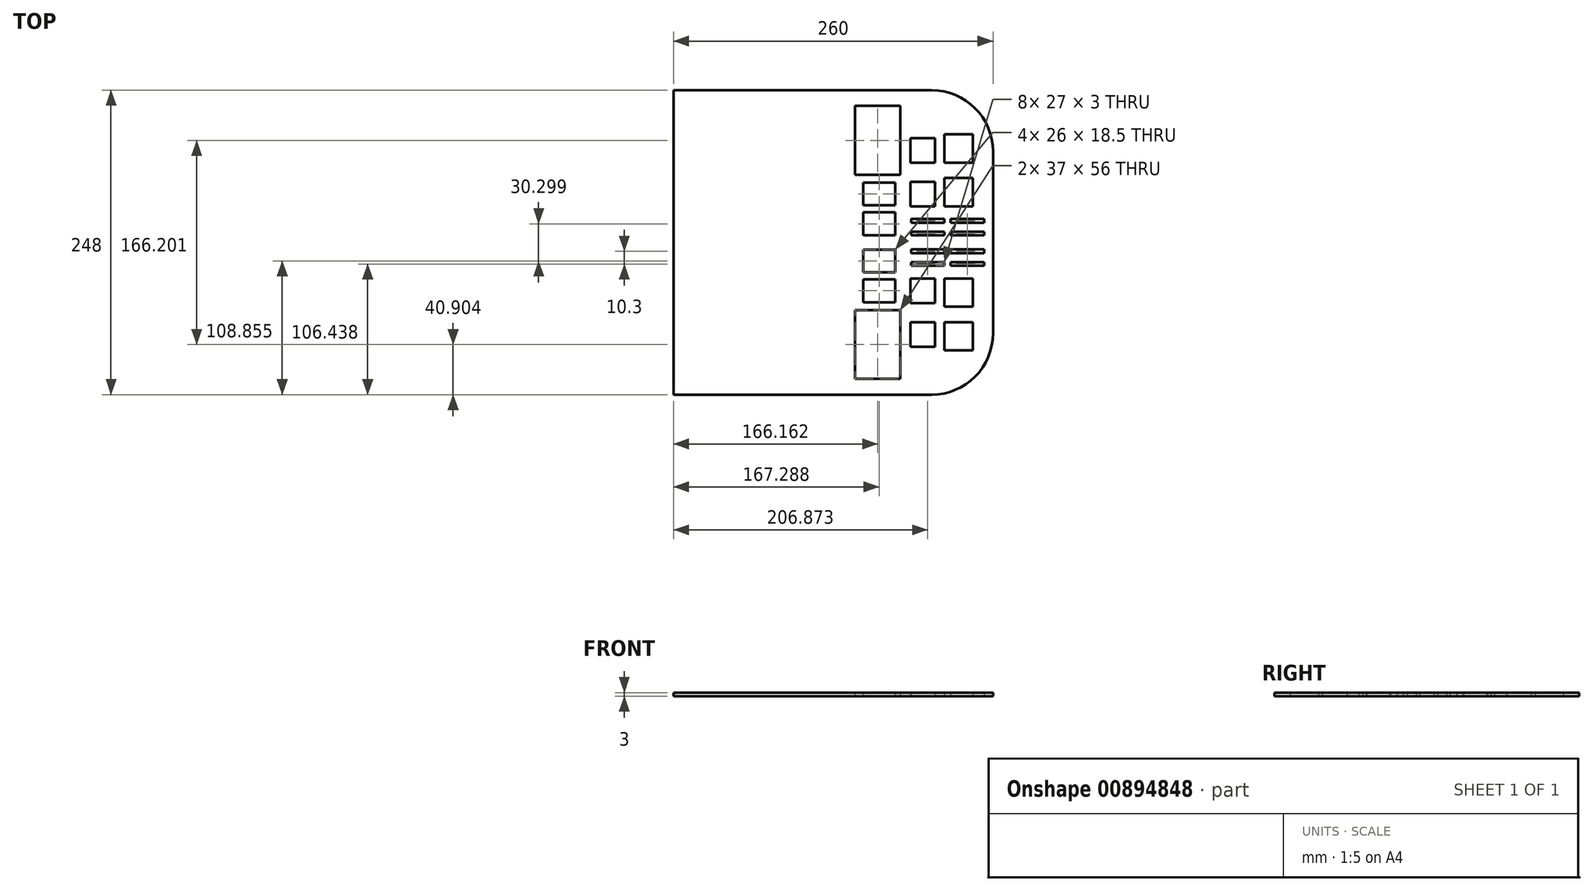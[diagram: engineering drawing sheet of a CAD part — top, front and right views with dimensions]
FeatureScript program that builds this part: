
annotation { "Feature Type Name" : "Feature", "Feature Type Description" : "" }
export const myFeature = defineFeature(function(context is Context, id is Id, definition is map)
    precondition{}
    {
        {
            var Q0;
            Q0=qCreatedBy(makeId("Top.planeOp"),FACE);
            var sketch = newSketch(context, id + "F0", { "sketchPlane" : qUnion([Q0])});
            skLineSegment(sketch, "E0", {"start": v(-246.73, 107.93) * mm, "end": v(-246.73, -140.07) * mm});
            skLineSegment(sketch, "E1", {"start": v(-246.73, -140.07) * mm, "end": v(-36.73, -140.07) * mm});
            skLineSegment(sketch, "E2", {"start": v(13.27, -90.07) * mm, "end": v(13.27, 57.93) * mm});
            skLineSegment(sketch, "E3", {"start": v(-36.73, 107.93) * mm, "end": v(-246.73, 107.93) * mm});
            skPoint(sketch, "E4.visualSharp", {"position": v(13.27, 107.93) * mm});
            skArc(sketch, "E4.filletArc", {"start": v(13.27, 57.93) * mm, "mid": v(-1.38, 93.29) * mm, "end": v(-36.73, 107.93) * mm});
            skPoint(sketch, "E5.visualSharp", {"position": v(13.27, -140.07) * mm});
            skArc(sketch, "E5.filletArc", {"start": v(-36.73, -140.07) * mm, "mid": v(-1.38, -125.42) * mm, "end": v(13.27, -90.07) * mm});
            skLineSegment(sketch, "E6.bottom", {"start": v(-53.91, 68.92) * mm, "end": v(-33.91, 68.92) * mm});
            skLineSegment(sketch, "E6.top", {"start": v(-53.91, 48.92) * mm, "end": v(-33.91, 48.92) * mm});
            skLineSegment(sketch, "E6.left", {"start": v(-53.91, 68.92) * mm, "end": v(-53.91, 48.92) * mm});
            skLineSegment(sketch, "E6.right", {"start": v(-33.91, 68.92) * mm, "end": v(-33.91, 48.92) * mm});
            skLineSegment(sketch, "E7.bottom", {"start": v(-26.23, 71.92) * mm, "end": v(-3.23, 71.92) * mm});
            skLineSegment(sketch, "E7.top", {"start": v(-26.23, 48.92) * mm, "end": v(-3.23, 48.92) * mm});
            skLineSegment(sketch, "E7.left", {"start": v(-26.23, 71.92) * mm, "end": v(-26.23, 48.92) * mm});
            skLineSegment(sketch, "E7.right", {"start": v(-3.23, 71.92) * mm, "end": v(-3.23, 48.92) * mm});
            skLineSegment(sketch, "E8.bottom", {"start": v(-53.91, 33.3) * mm, "end": v(-33.91, 33.3) * mm});
            skLineSegment(sketch, "E8.top", {"start": v(-53.91, 13.3) * mm, "end": v(-33.91, 13.3) * mm});
            skLineSegment(sketch, "E8.left", {"start": v(-53.91, 33.3) * mm, "end": v(-53.91, 13.3) * mm});
            skLineSegment(sketch, "E8.right", {"start": v(-33.91, 33.3) * mm, "end": v(-33.91, 13.3) * mm});
            skLineSegment(sketch, "E9.bottom", {"start": v(-26.23, 36.3) * mm, "end": v(-3.23, 36.3) * mm});
            skLineSegment(sketch, "E9.top", {"start": v(-26.23, 13.3) * mm, "end": v(-3.23, 13.3) * mm});
            skLineSegment(sketch, "E9.left", {"start": v(-26.23, 36.3) * mm, "end": v(-26.23, 13.3) * mm});
            skLineSegment(sketch, "E9.right", {"start": v(-3.23, 36.3) * mm, "end": v(-3.23, 13.3) * mm});
            skLineSegment(sketch, "E10", {"start": v(-53.91, 48.92) * mm, "end": v(-53.91, 33.3) * mm, "construction": true});
            skLineSegment(sketch, "E11", {"start": v(-246.73, -16.07) * mm, "end": v(13.27, -16.07) * mm, "construction": true});
            skLineSegment(sketch, "E12.bottom", {"start": v(-99.07, 95.03) * mm, "end": v(-62.07, 95.03) * mm});
            skLineSegment(sketch, "E12.top", {"start": v(-99.07, 39.03) * mm, "end": v(-62.07, 39.03) * mm});
            skLineSegment(sketch, "E12.left", {"start": v(-99.07, 95.03) * mm, "end": v(-99.07, 39.03) * mm});
            skLineSegment(sketch, "E12.right", {"start": v(-62.07, 95.03) * mm, "end": v(-62.07, 39.03) * mm});
            skLineSegment(sketch, "E13.bottom", {"start": v(-92.3, 32.6) * mm, "end": v(-66.3, 32.6) * mm});
            skLineSegment(sketch, "E13.top", {"start": v(-92.3, 14.1) * mm, "end": v(-66.3, 14.1) * mm});
            skLineSegment(sketch, "E13.left", {"start": v(-92.3, 32.6) * mm, "end": v(-92.3, 14.1) * mm});
            skLineSegment(sketch, "E13.right", {"start": v(-66.3, 32.6) * mm, "end": v(-66.3, 14.1) * mm});
            skLineSegment(sketch, "E14.bottom", {"start": v(-92.44, 8.33) * mm, "end": v(-66.44, 8.33) * mm});
            skLineSegment(sketch, "E14.top", {"start": v(-92.44, -10.17) * mm, "end": v(-66.44, -10.17) * mm});
            skLineSegment(sketch, "E14.left", {"start": v(-92.44, 8.33) * mm, "end": v(-92.44, -10.17) * mm});
            skLineSegment(sketch, "E14.right", {"start": v(-66.44, 8.33) * mm, "end": v(-66.44, -10.17) * mm});
            skLineSegment(sketch, "E15.bottom", {"start": v(-53.36, 3) * mm, "end": v(-26.36, 3) * mm});
            skLineSegment(sketch, "E15.top", {"start": v(-53.36, 0) * mm, "end": v(-26.36, 0) * mm});
            skLineSegment(sketch, "E15.left", {"start": v(-53.36, 3) * mm, "end": v(-53.36, 0) * mm});
            skLineSegment(sketch, "E15.right", {"start": v(-26.36, 3) * mm, "end": v(-26.36, 0) * mm});
            skLineSegment(sketch, "E16.0.1.0", {"start": v(-53.36, -10.3) * mm, "end": v(-26.36, -10.3) * mm});
            skLineSegment(sketch, "E16.0.1.1", {"start": v(-53.36, -7.3) * mm, "end": v(-53.36, -10.3) * mm});
            skLineSegment(sketch, "E16.0.1.2", {"start": v(-53.36, -7.3) * mm, "end": v(-26.36, -7.3) * mm});
            skLineSegment(sketch, "E16.0.1.3", {"start": v(-26.36, -7.3) * mm, "end": v(-26.36, -10.3) * mm});
            skLineSegment(sketch, "E16.1.0.0", {"start": v(-21.06, 0) * mm, "end": v(5.94, 0) * mm});
            skLineSegment(sketch, "E16.1.0.1", {"start": v(-21.06, 3) * mm, "end": v(-21.06, 0) * mm});
            skLineSegment(sketch, "E16.1.0.2", {"start": v(-21.06, 3) * mm, "end": v(5.94, 3) * mm});
            skLineSegment(sketch, "E16.1.0.3", {"start": v(5.94, 3) * mm, "end": v(5.94, 0) * mm});
            skLineSegment(sketch, "E16.1.1.0", {"start": v(-21.06, -10.3) * mm, "end": v(5.94, -10.3) * mm});
            skLineSegment(sketch, "E16.1.1.1", {"start": v(-21.06, -7.3) * mm, "end": v(-21.06, -10.3) * mm});
            skLineSegment(sketch, "E16.1.1.2", {"start": v(-21.06, -7.3) * mm, "end": v(5.94, -7.3) * mm});
            skLineSegment(sketch, "E16.1.1.3", {"start": v(5.94, -7.3) * mm, "end": v(5.94, -10.3) * mm});
            skLineSegment(sketch, "E16.direction1", {"start": v(-53.36, 0) * mm, "end": v(-21.06, 0) * mm, "construction": true});
            skLineSegment(sketch, "E16.direction2", {"start": v(-53.36, 0) * mm, "end": v(-53.36, -10.3) * mm, "construction": true});
            skLineSegment(sketch, "E17.MirrorCS", {"start": v(-53.36, -24.83) * mm, "end": v(-53.36, -21.83) * mm});
            skLineSegment(sketch, "E18.MirrorCS", {"start": v(-21.06, -35.13) * mm, "end": v(-21.06, -32.13) * mm});
            skLineSegment(sketch, "E19.MirrorCS", {"start": v(-26.36, -35.13) * mm, "end": v(-26.36, -32.13) * mm});
            skLineSegment(sketch, "E20.MirrorCS", {"start": v(-53.36, -35.13) * mm, "end": v(-53.36, -32.13) * mm});
            skLineSegment(sketch, "E21.MirrorCS", {"start": v(5.94, -24.83) * mm, "end": v(5.94, -21.83) * mm});
            skLineSegment(sketch, "E22.MirrorCS", {"start": v(-21.06, -24.83) * mm, "end": v(-21.06, -21.83) * mm});
            skLineSegment(sketch, "E23.MirrorCS", {"start": v(5.94, -35.13) * mm, "end": v(5.94, -32.13) * mm});
            skLineSegment(sketch, "E24.MirrorCS", {"start": v(-26.36, -24.83) * mm, "end": v(-26.36, -21.83) * mm});
            skLineSegment(sketch, "E25.MirrorCS", {"start": v(-53.36, -32.13) * mm, "end": v(-26.36, -32.13) * mm});
            skLineSegment(sketch, "E26.MirrorCS", {"start": v(-53.36, -32.13) * mm, "end": v(-53.36, -21.83) * mm, "construction": true});
            skLineSegment(sketch, "E27.MirrorCS", {"start": v(-53.91, -65.42) * mm, "end": v(-33.91, -65.42) * mm});
            skLineSegment(sketch, "E28.MirrorCS", {"start": v(-3.23, -104.06) * mm, "end": v(-3.23, -81.06) * mm});
            skLineSegment(sketch, "E29.MirrorCS", {"start": v(-53.91, -45.42) * mm, "end": v(-33.91, -45.42) * mm});
            skLineSegment(sketch, "E30.MirrorCS", {"start": v(-26.23, -104.06) * mm, "end": v(-26.23, -81.06) * mm});
            skLineSegment(sketch, "E31.MirrorCS", {"start": v(-26.23, -81.06) * mm, "end": v(-3.23, -81.06) * mm});
            skLineSegment(sketch, "E32.MirrorCS", {"start": v(-53.91, -65.42) * mm, "end": v(-53.91, -45.42) * mm});
            skLineSegment(sketch, "E33.MirrorCS", {"start": v(-53.91, -101.06) * mm, "end": v(-53.91, -81.06) * mm});
            skLineSegment(sketch, "E34.MirrorCS", {"start": v(-21.06, -24.83) * mm, "end": v(5.94, -24.83) * mm});
            skLineSegment(sketch, "E35.MirrorCS", {"start": v(-53.36, -35.13) * mm, "end": v(-26.36, -35.13) * mm});
            skLineSegment(sketch, "E36.MirrorCS", {"start": v(-99.07, -71.17) * mm, "end": v(-62.07, -71.17) * mm});
            skLineSegment(sketch, "E37.MirrorCS", {"start": v(-3.23, -68.42) * mm, "end": v(-3.23, -45.42) * mm});
            skLineSegment(sketch, "E38.MirrorCS", {"start": v(-21.06, -35.13) * mm, "end": v(5.94, -35.13) * mm});
            skLineSegment(sketch, "E39.MirrorCS", {"start": v(-21.06, -21.83) * mm, "end": v(5.94, -21.83) * mm});
            skLineSegment(sketch, "E40.MirrorCS", {"start": v(-53.36, -21.83) * mm, "end": v(-26.36, -21.83) * mm});
            skLineSegment(sketch, "E41.MirrorCS", {"start": v(-92.44, -40.47) * mm, "end": v(-92.44, -21.97) * mm});
            skLineSegment(sketch, "E42.MirrorCS", {"start": v(-99.07, -127.17) * mm, "end": v(-99.07, -71.17) * mm});
            skLineSegment(sketch, "E43.MirrorCS", {"start": v(-26.23, -104.06) * mm, "end": v(-3.23, -104.06) * mm});
            skLineSegment(sketch, "E44.MirrorCS", {"start": v(-92.3, -64.73) * mm, "end": v(-92.3, -46.23) * mm});
            skLineSegment(sketch, "E45.MirrorCS", {"start": v(-53.36, -32.13) * mm, "end": v(-21.06, -32.13) * mm, "construction": true});
            skLineSegment(sketch, "E46.MirrorCS", {"start": v(-53.91, -81.06) * mm, "end": v(-53.91, -65.42) * mm, "construction": true});
            skLineSegment(sketch, "E47.MirrorCS", {"start": v(-53.91, -101.06) * mm, "end": v(-33.91, -101.06) * mm});
            skLineSegment(sketch, "E48.MirrorCS", {"start": v(-62.07, -127.17) * mm, "end": v(-62.07, -71.17) * mm});
            skLineSegment(sketch, "E49.MirrorCS", {"start": v(-53.91, -81.06) * mm, "end": v(-33.91, -81.06) * mm});
            skLineSegment(sketch, "E50.MirrorCS", {"start": v(-92.3, -64.73) * mm, "end": v(-66.3, -64.73) * mm});
            skLineSegment(sketch, "E51.MirrorCS", {"start": v(-53.36, -24.83) * mm, "end": v(-26.36, -24.83) * mm});
            skLineSegment(sketch, "E52.MirrorCS", {"start": v(-92.44, -40.47) * mm, "end": v(-66.44, -40.47) * mm});
            skLineSegment(sketch, "E53.MirrorCS", {"start": v(-21.06, -32.13) * mm, "end": v(5.94, -32.13) * mm});
            skLineSegment(sketch, "E54.MirrorCS", {"start": v(-92.44, -21.97) * mm, "end": v(-66.44, -21.97) * mm});
            skLineSegment(sketch, "E55.MirrorCS", {"start": v(-66.3, -64.73) * mm, "end": v(-66.3, -46.23) * mm});
            skLineSegment(sketch, "E56.MirrorCS", {"start": v(-26.23, -68.42) * mm, "end": v(-3.23, -68.42) * mm});
            skLineSegment(sketch, "E57.MirrorCS", {"start": v(-33.91, -65.42) * mm, "end": v(-33.91, -45.42) * mm});
            skLineSegment(sketch, "E58.MirrorCS", {"start": v(-26.23, -45.42) * mm, "end": v(-3.23, -45.42) * mm});
            skLineSegment(sketch, "E59.MirrorCS", {"start": v(-99.07, -127.17) * mm, "end": v(-62.07, -127.17) * mm});
            skLineSegment(sketch, "E60.MirrorCS", {"start": v(-92.3, -46.23) * mm, "end": v(-66.3, -46.23) * mm});
            skLineSegment(sketch, "E61.MirrorCS", {"start": v(-26.23, -68.42) * mm, "end": v(-26.23, -45.42) * mm});
            skLineSegment(sketch, "E62.MirrorCS", {"start": v(-33.91, -101.06) * mm, "end": v(-33.91, -81.06) * mm});
            skLineSegment(sketch, "E63.MirrorCS", {"start": v(-66.44, -40.47) * mm, "end": v(-66.44, -21.97) * mm});
            skSolve(sketch);
        }
        {
            var Q0;
            Q0=makeQuery(id+"F0.imprint","IMPRINT",FACE,{"disambiguationData":[TD([[makeQuery(id+"F0.imprint","IMPRINT",EDGE,{"derivedFrom":sQuery(id+"F0.wireOp",EDGE,"E0")}),1.0]])]});
            extrude(context, id + "F1", {"entities" : qUnion([Q0]), "depth" : 3 * mm, "offsetDistance" : 25 * mm, "symmetric" : true});
        }
    });
